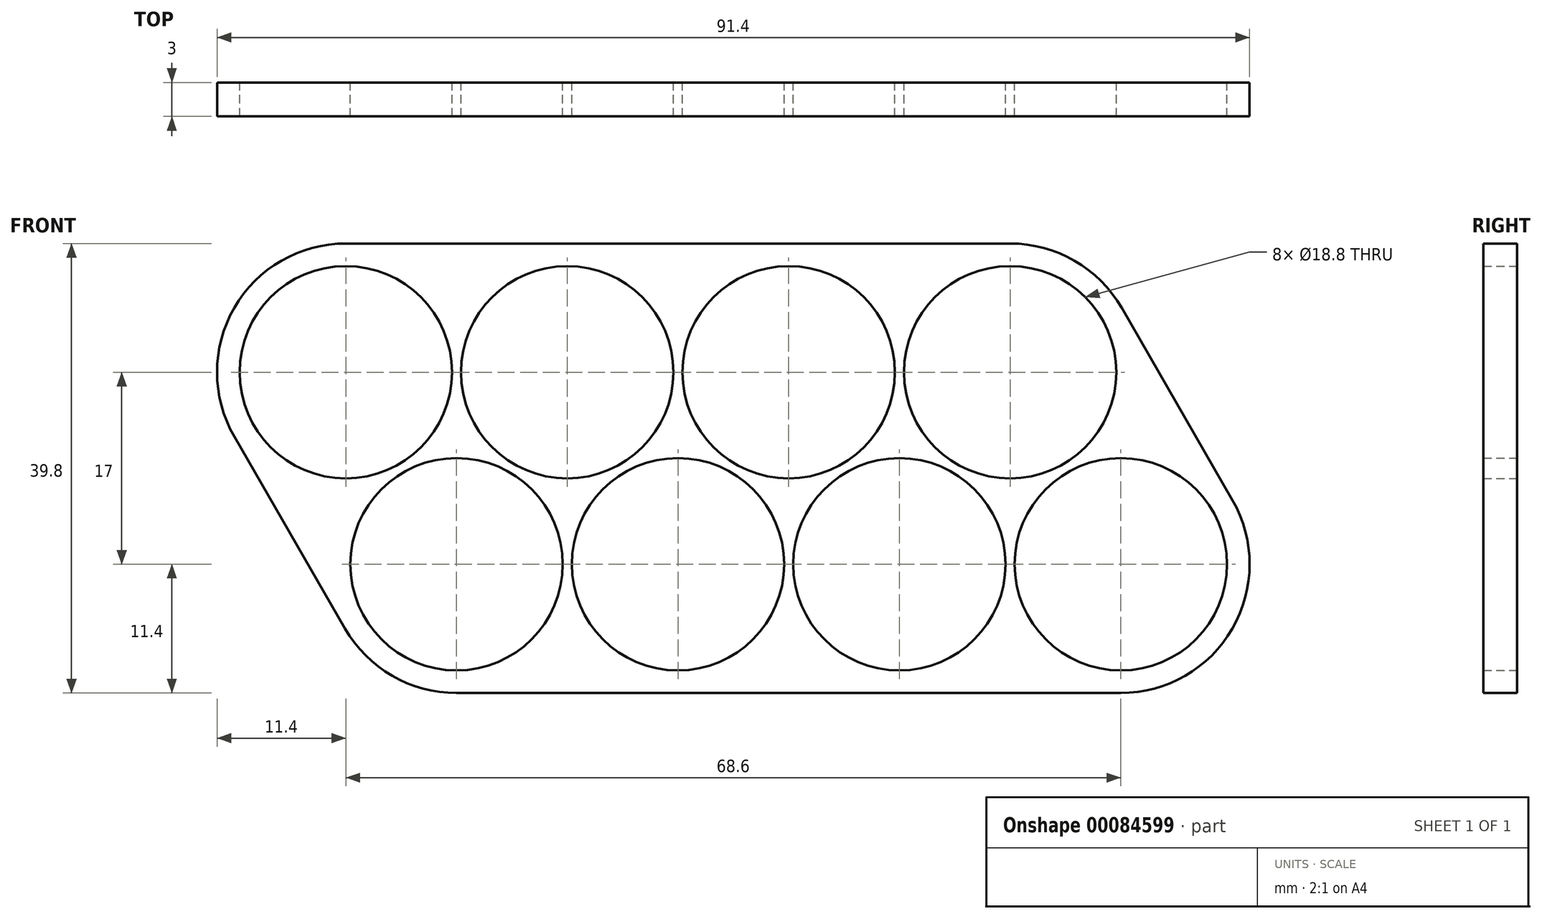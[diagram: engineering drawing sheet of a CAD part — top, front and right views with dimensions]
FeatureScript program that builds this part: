
annotation { "Feature Type Name" : "Feature", "Feature Type Description" : "" }
export const myFeature = defineFeature(function(context is Context, id is Id, definition is map)
    precondition{}
    {
        {
            var Q0;
            Q0=qCreatedBy(makeId("Front.planeOp"),FACE);
            var sketch = newSketch(context, id + "F0", { "sketchPlane" : qUnion([Q0]) });
            skCircle(sketch, "E0", {"center": v(0, 0) * mm, "radius": 9.4 * mm});
            skCircle(sketch, "E1.1.0.0", {"center": v(19.6, 0) * mm, "radius": 9.4 * mm});
            skCircle(sketch, "E1.2.0.0", {"center": v(39.2, 0) * mm, "radius": 9.4 * mm});
            skCircle(sketch, "E1.3.0.0", {"center": v(58.8, 0) * mm, "radius": 9.4 * mm});
            skLineSegment(sketch, "E1.direction1", {"start": v(0, 0) * mm, "end": v(19.6, 0) * mm, "construction": true});
            skLineSegment(sketch, "E2", {"start": v(0, -17) * mm, "end": v(73.2, -17) * mm, "construction": true});
            skLineSegment(sketch, "E3", {"start": v(9.8, 0) * mm, "end": v(9.8, -17) * mm, "construction": true});
            skCircle(sketch, "E4", {"center": v(9.8, -17) * mm, "radius": 9.4 * mm});
            skCircle(sketch, "E5.1.0.0", {"center": v(29.4, -17) * mm, "radius": 9.4 * mm});
            skCircle(sketch, "E5.2.0.0", {"center": v(49, -17) * mm, "radius": 9.4 * mm});
            skCircle(sketch, "E5.3.0.0", {"center": v(68.6, -17) * mm, "radius": 9.4 * mm});
            skLineSegment(sketch, "E5.direction1", {"start": v(9.8, -17) * mm, "end": v(29.4, -17) * mm, "construction": true});
            skLineSegment(sketch, "E6", {"start": v(-8.14, -4.7) * mm, "end": v(1.66, -21.7) * mm});
            skLineSegment(sketch, "E7", {"start": v(0, 9.4) * mm, "end": v(58.8, 9.4) * mm});
            skLineSegment(sketch, "E8", {"start": v(9.8, -17) * mm, "end": v(9.8, -26.4) * mm, "construction": true});
            skLineSegment(sketch, "E9", {"start": v(68.6, -17) * mm, "end": v(68.6, -26.4) * mm, "construction": true});
            skLineSegment(sketch, "E10", {"start": v(9.8, -26.4) * mm, "end": v(68.6, -26.4) * mm});
            skLineSegment(sketch, "E11", {"start": v(66.94, 4.7) * mm, "end": v(76.74, -12.3) * mm});
            skArc(sketch, "E12", {"start": v(58.8, 9.4) * mm, "mid": v(63.5, 8.14) * mm, "end": v(66.94, 4.7) * mm});
            skArc(sketch, "E13", {"start": v(76.74, -12.3) * mm, "mid": v(76.74, -21.7) * mm, "end": v(68.6, -26.4) * mm});
            skArc(sketch, "E14", {"start": v(9.8, -26.4) * mm, "mid": v(5.1, -25.14) * mm, "end": v(1.66, -21.7) * mm});
            skArc(sketch, "E15", {"start": v(-8.14, -4.7) * mm, "mid": v(-8.14, 4.7) * mm, "end": v(0, 9.4) * mm});
            skArc(sketch, "E16.0", {"start": v(0, 11.4) * mm, "mid": v(-9.87, 5.7) * mm, "end": v(-9.88, -5.7) * mm});
            skLineSegment(sketch, "E17.0", {"start": v(0, 11.4) * mm, "end": v(58.8, 11.4) * mm});
            skArc(sketch, "E18.0", {"start": v(68.68, 5.7) * mm, "mid": v(64.5, 9.87) * mm, "end": v(58.8, 11.4) * mm});
            skLineSegment(sketch, "E19.0", {"start": v(68.68, 5.7) * mm, "end": v(78.48, -11.3) * mm});
            skLineSegment(sketch, "E20.0", {"start": v(9.8, -28.4) * mm, "end": v(68.6, -28.4) * mm});
            skLineSegment(sketch, "E21.0", {"start": v(-9.88, -5.7) * mm, "end": v(-0.08, -22.7) * mm});
            skArc(sketch, "E22.0", {"start": v(-0.08, -22.7) * mm, "mid": v(4.1, -26.87) * mm, "end": v(9.8, -28.4) * mm});
            skArc(sketch, "E23.0", {"start": v(68.6, -28.4) * mm, "mid": v(78.47, -22.7) * mm, "end": v(78.48, -11.3) * mm});
            skArc(sketch, "E24.trimOffspring", {"start": v(9.8, -5.82) * mm, "mid": v(9.87, -5.71) * mm, "end": v(9.93, -5.6) * mm});
            skArc(sketch, "E25.trimOffspring", {"start": v(9.93, -5.6) * mm, "mid": v(9.86, -5.6) * mm, "end": v(9.8, -5.6) * mm});
            skLineSegment(sketch, "E26", {"start": v(39.2, 0) * mm, "end": v(49, -17) * mm, "construction": true});
            skLineSegment(sketch, "E27", {"start": v(49, -17) * mm, "end": v(55.57, -28.4) * mm, "construction": true});
            skLineSegment(sketch, "E28", {"start": v(39.2, 0) * mm, "end": v(32.63, 11.4) * mm, "construction": true});
            skSolve(sketch);
        }
        {
            var Q0;
            Q0 = qSketchRegion(id + "F0", true);
            var Q1;
            {var subQ3=sQuery(id+"F0.wireOp",EDGE,"E1.1.0.0");Q1=makeQuery(id+"F0.imprint","IMPRINT",FACE,{"disambiguationData":[TD([[makeQuery(id+"F0.imprint","IMPRINT",EDGE,{"derivedFrom":subQ3}),-1.0]])]});}
            extrude(context, id + "F1", {"entities" : qUnion([Q0, Q1]), "depth" : 3 * mm});
        }
    });
